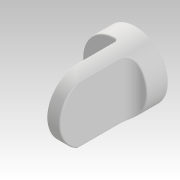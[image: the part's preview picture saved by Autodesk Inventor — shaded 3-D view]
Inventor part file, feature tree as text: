
AUTODESK INVENTOR PART (.ipt)
format: ipt  version: 2020 (Build 240168000, 168)  size: 449,536 bytes
history: native  units: mm
features: extrude x17, sketch x17, fillet x4, projected_geometry x4, plane x1, chamfer x1
ambient origin geometry x8: Origin, YZ Plane, XZ Plane, XY Plane, X Axis, Y Axis, Z Axis, Center Point
bodies: Solid1 (feature_tree)
feature tree (44):
  extrude  "Extrusion1"  Depth=90.0mm
  extrude  "Extrusion2"  Depth=53.0mm
  extrude  "Extrusion3"  Depth=29.0mm TaperAngle=0.0deg
  extrude  "Extrusion4"  Depth=42.0mm
  extrude  "Extrusion5"  Depth=86.0mm
  fillet  "Fillet2"  Radius=59.0mm
  extrude  "Extrusion6"  Depth=25.0mm TaperAngle=0.0deg
  extrude  "Extrusion7"  Depth=10.0mm TaperAngle=0.0deg
  extrude  "Extrusion8"  Depth=7.0mm TaperAngle=0.0deg
  plane  "Work Plane1"
  extrude  "Extrusion9"  Depth=13.0mm
  extrude  "Extrusion10"  Depth=7.5mm TaperAngle=0.0deg
  extrude  "Extrusion11"  Depth=7.5mm
  extrude  "Extrusion12"  Depth=7.5mm TaperAngle=0.0deg
  fillet  "Fillet3"  Radius=7.5mm
  fillet  "Fillet4"  Radius=7.5mm
  extrude  "Extrusion13"  Depth=2.0mm
  extrude  "Extrusion14"  Depth=10.0mm TaperAngle=0.0deg
  fillet  "Fillet5"  Radius=3.0mm
  chamfer  "Chamfer2"  Distance=0.5mm Angle=45.0deg
  extrude  "Extrusion15"  Depth=50.0mm
  extrude  "Extrusion16"  Depth=10.0mm TaperAngle=0.0deg
  extrude  "Extrusion17"  Depth=1.0mm
  sketch  "Sketch1"  dims[d0=50.0mm d1=90.0mm]
  sketch  "Sketch2"  dims[d2=19.0mm d3=0.0mm d4=53.0mm]
  sketch  "Sketch3"  dims[d5=90.0mm d7=29.0mm d8=0.0mm]
  sketch  "Sketch4"  dims[d9=12.5mm d10=42.0mm]
  sketch  "Sketch5"  dims[d11=27.0mm d12=0.0mm d15=86.0mm d16=59.0mm]
  projected_geometry  "Projected Loop1"
  projected_geometry  "Projected Loop2"
  sketch  "Sketch6"  dims[d17=3.5mm d18=0.0mm d19=25.0mm d20=0.0mm]
  sketch  "Sketch7"  dims[d21=15.0mm d22=10.0mm d23=0.0mm]
  sketch  "Sketch8"  dims[d24=34.9mm d25=7.0mm d26=0.0mm]
  sketch  "Sketch9"  dims[d27=5.1mm d28=13.0mm]
  sketch  "Sketch10"  dims[d29=60.0mm d31=360.0deg d33=7.5mm d34=0.0mm]
  sketch  "Sketch11"  dims[d35=-10.0mm d36=7.5mm]
  sketch  "Sketch12"  dims[d37=7.5mm d38=0.0mm d39=7.5mm d40=0.0mm d41=7.5mm d42=0.0mm d43=7.5mm d44=0.0mm]
  sketch  "Sketch13"  dims[d45=5.0mm d46=2.0mm]
  projected_geometry  "Projected Loop3"
  sketch  "Sketch14"  dims[d50=10.0mm d51=0.0mm d52=10.0mm d53=0.0mm d54=3.0mm]
  projected_geometry  "Projected Loop4"
  sketch  "Sketch15"  dims[d55=2.0mm d56=0.5mm d57=2.0mm d58=45.0deg]
  sketch  "Sketch16"  dims[d59=3.0mm d60=0.0mm d61=50.0mm]
  sketch  "Sketch17"  dims[d62=5.0mm d63=10.0mm d64=0.0mm d65=59.0mm d66=86.0mm d67=1.0mm d68=0.0mm]
